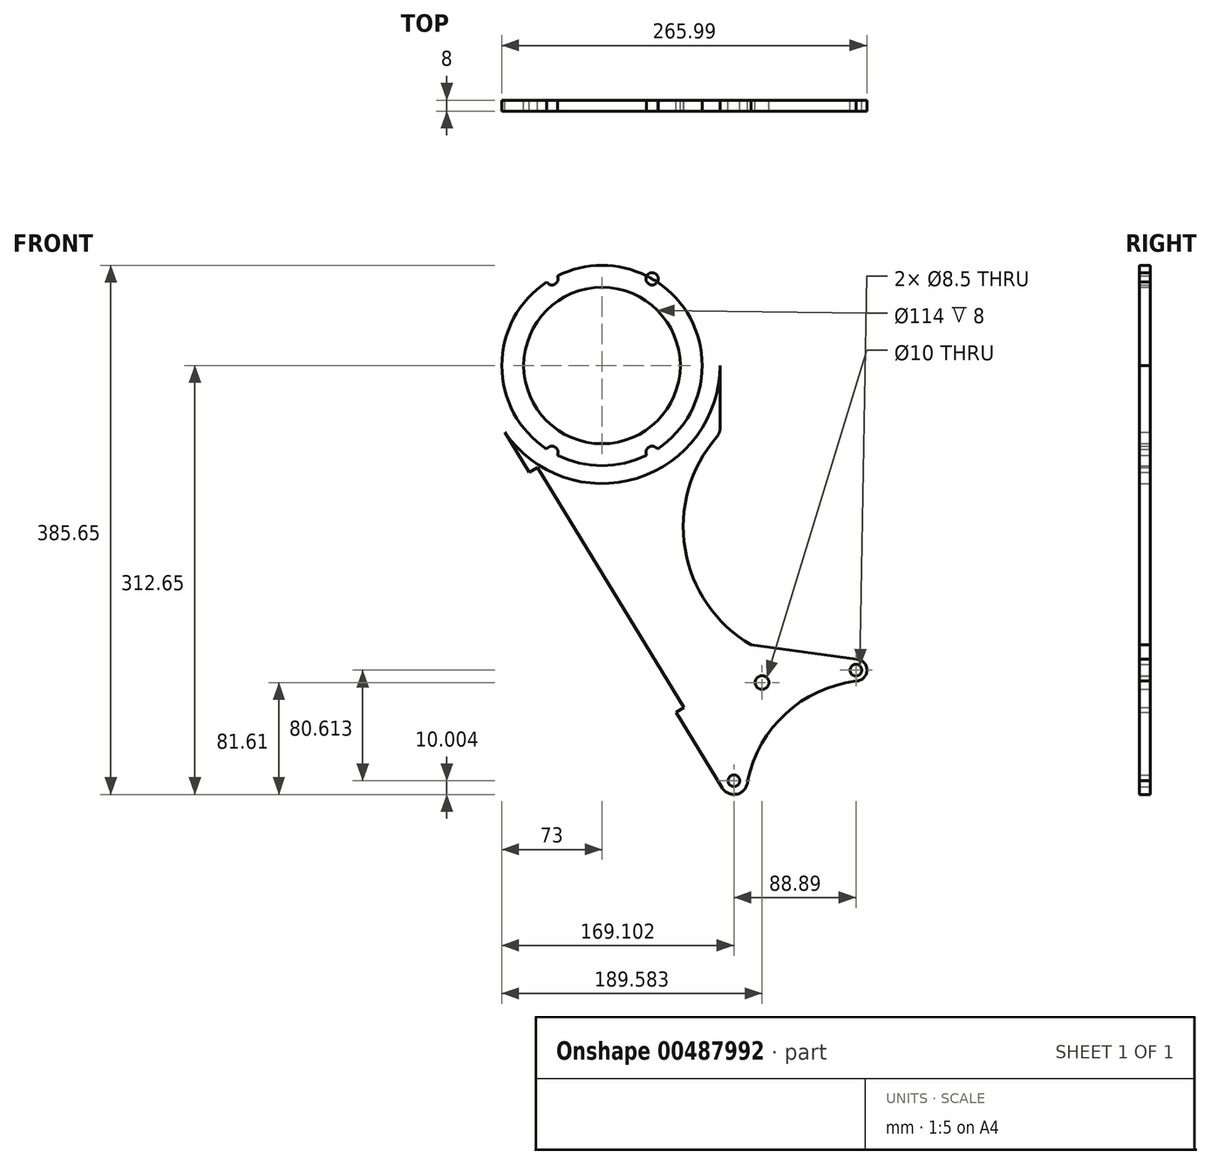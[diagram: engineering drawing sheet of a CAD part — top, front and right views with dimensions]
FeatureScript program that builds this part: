
annotation { "Feature Type Name" : "Feature", "Feature Type Description" : "" }
export const myFeature = defineFeature(function(context is Context, id is Id, definition is map)
    precondition{}
    {
        {
            var Q0;
            Q0=qCreatedBy(makeId("Front.planeOp"),FACE);
            var sketch = newSketch(context, id + "F0", { "sketchPlane" : qUnion([Q0])});
            skCircle(sketch, "E0", {"center": v(0, 0) * mm, "radius": 57 * mm});
            skCircle(sketch, "E1", {"center": v(0, 0) * mm, "radius": 73 * mm});
            skCircle(sketch, "E2", {"center": v(0, 0) * mm, "radius": 86 * mm});
            skPoint(sketch, "E3", {"position": v(-73, 0) * mm});
            skPoint(sketch, "E4", {"position": v(73, 0) * mm});
            skPoint(sketch, "E5.1.0", {"position": v(-36.5, -63.22) * mm});
            skPoint(sketch, "E5.2.0", {"position": v(36.5, -63.22) * mm});
            skPoint(sketch, "E6.0.4.0", {"position": v(36.5, 63.22) * mm});
            skPoint(sketch, "E6.0.5.0", {"position": v(-36.5, 63.22) * mm});
            skCircle(sketch, "E7", {"center": v(-36.5, -63.22) * mm, "radius": 4.5 * mm});
            skCircle(sketch, "E8", {"center": v(36.5, -63.22) * mm, "radius": 4.5 * mm});
            skCircle(sketch, "E9", {"center": v(-36.5, 63.22) * mm, "radius": 4.5 * mm});
            skCircle(sketch, "E10", {"center": v(36.5, 63.22) * mm, "radius": 4.5 * mm});
            skCircle(sketch, "E11", {"center": v(185, -222.03) * mm, "radius": 4.25 * mm});
            skCircle(sketch, "E12", {"center": v(116.58, -231.04) * mm, "radius": 5 * mm});
            skCircle(sketch, "E13", {"center": v(96.1, -302.65) * mm, "radius": 4.25 * mm});
            skCircle(sketch, "E14", {"center": v(96.1, -302.65) * mm, "radius": 10 * mm});
            skCircle(sketch, "E15", {"center": v(185, -222.03) * mm, "radius": 8 * mm});
            skArc(sketch, "E16", {"start": v(185, -230.03) * mm, "mid": v(133.87, -253.7) * mm, "end": v(106.1, -302.73) * mm});
            skLineSegment(sketch, "E17", {"start": v(86, 0) * mm, "end": v(86, -45.55) * mm});
            skLineSegment(sketch, "E18", {"start": v(-75.68, -40.84) * mm, "end": v(-53, -77.96) * mm});
            skLineSegment(sketch, "E19", {"start": v(116.58, -231.04) * mm, "end": v(116.58, -226.04) * mm});
            skLineSegment(sketch, "E20", {"start": v(185.05, -214.03) * mm, "end": v(108.53, -203.52) * mm});
            skArc(sketch, "E21", {"start": v(83.56, -52.1) * mm, "mid": v(60.56, -133.66) * mm, "end": v(108.53, -203.52) * mm});
            skArc(sketch, "E22.filletArc", {"start": v(83.56, -52.1) * mm, "mid": v(85.37, -49.04) * mm, "end": v(86, -45.55) * mm});
            skLineSegment(sketch, "E23.trimOffspring", {"start": v(68.1, -76.26) * mm, "end": v(75.4, -62.33) * mm});
            skLineSegment(sketch, "E24.trimOffspring", {"start": v(93.13, -293.1) * mm, "end": v(96.1, -302.65) * mm});
            skLineSegment(sketch, "E25", {"start": v(-53, -77.96) * mm, "end": v(-47.12, -74.37) * mm});
            skLineSegment(sketch, "E26", {"start": v(-47.12, -74.37) * mm, "end": v(59.82, -249.27) * mm});
            skLineSegment(sketch, "E27", {"start": v(59.82, -249.27) * mm, "end": v(53.94, -252.86) * mm});
            skLineSegment(sketch, "E28.trimOffspring", {"start": v(53.94, -252.86) * mm, "end": v(87.57, -307.86) * mm});
            skSolve(sketch);
        }
        {
            var Q0;
            {var subQ5=sQuery(id+"F0.wireOp",EDGE,"IF3RerSK-Avve-Ym9k-tSXP-Sf0ZYguiSfRi");var subQ6=sQuery(id+"F0.wireOp",EDGE,"E0");var subQ7=makeQuery(id+"F0.imprint","INTERSECT",VERTEX,{"disambiguationData":[OD(0.0)],"derivedFrom":[subQ6,subQ5]});Q0=makeQuery(id+"F0.imprint","IMPRINT",FACE,{"disambiguationData":[TD([[makeQuery(id+"F0.imprint","IMPRINT",EDGE,{"disambiguationData":[TD([[subQ7,-1.0]])],"derivedFrom":subQ6}),-1.0]])]});}
            var Q1;
            {var subQ3=sQuery(id+"F0.wireOp",EDGE,"IF3RerSK-Avve-Ym9k-tSXP-Sf0ZYguiSfRi");var subQ8=sQuery(id+"F0.wireOp",EDGE,"E0");var subQ9=makeQuery(id+"F0.imprint","INTERSECT",VERTEX,{"disambiguationData":[OD(0.0)],"derivedFrom":[subQ8,subQ3]});Q1=makeQuery(id+"F0.imprint","IMPRINT",FACE,{"disambiguationData":[TD([[makeQuery(id+"F0.imprint","IMPRINT",EDGE,{"disambiguationData":[TD([[subQ9,1.0]])],"derivedFrom":subQ8}),-1.0]])]});}
            var Q2;
            Q2=makeQuery(id+"F0.imprint","IMPRINT",FACE,{"disambiguationData":[TD([[makeQuery(id+"F0.imprint","IMPRINT",EDGE,{"derivedFrom":sQuery(id+"F0.wireOp",EDGE,"E12")}),-1.0]])]});
            var Q3;
            {var subQ0=sQuery(id+"F0.wireOp",EDGE,"Hq9JJhjp-hlPl-h66M-fUjF-8FcOxtTSrp2Q");var subQ1=sQuery(id+"F0.wireOp",EDGE,"E2");var subQ2=makeQuery(id+"F0.imprint","INTERSECT",VERTEX,{"derivedFrom":[subQ1,subQ0]});Q3=makeQuery(id+"F0.imprint","IMPRINT",FACE,{"disambiguationData":[TD([[makeQuery(id+"F0.imprint","IMPRINT",EDGE,{"disambiguationData":[TD([[subQ2,-1.0]])],"derivedFrom":subQ1}),-1.0]])]});}
            var Q4;
            Q4=makeQuery(id+"F0.imprint","IMPRINT",FACE,{"disambiguationData":[TD([[makeQuery(id+"F0.imprint","IMPRINT",EDGE,{"derivedFrom":sQuery(id+"F0.wireOp",EDGE,"E13")}),-1.0]])]});
            var Q5;
            Q5=makeQuery(id+"F0.imprint","IMPRINT",FACE,{"disambiguationData":[TD([[makeQuery(id+"F0.imprint","IMPRINT",EDGE,{"derivedFrom":sQuery(id+"F0.wireOp",EDGE,"E11")}),-1.0]])]});
            var Q6;
            {var subQ1=sQuery(id+"F0.wireOp",EDGE,"E1");var subQ12=sQuery(id+"F0.wireOp",EDGE,"E10");var subQ13=makeQuery(id+"F0.imprint","INTERSECT",VERTEX,{"disambiguationData":[OD(0.0)],"derivedFrom":[subQ1,subQ12]});Q6=makeQuery(id+"F0.imprint","IMPRINT",FACE,{"disambiguationData":[TD([[makeQuery(id+"F0.imprint","IMPRINT",EDGE,{"disambiguationData":[TD([[subQ13,-1.0]])],"derivedFrom":subQ1}),-1.0]])]});}
            var Q7;
            Q7=makeQuery(id+"F0.imprint","IMPRINT",FACE,{"disambiguationData":[TD([[makeQuery(id+"F0.imprint","IMPRINT",EDGE,{"derivedFrom":sQuery(id+"F0.wireOp",EDGE,"E0")}),-1.0]])]});
            extrude(context, id + "F1", {"entities" : qUnion([Q0, Q1, Q2, Q3, Q4, Q5, Q6, Q7]), "depth" : 8 * mm, "offsetDistance" : 25 * mm});
        }
    });
